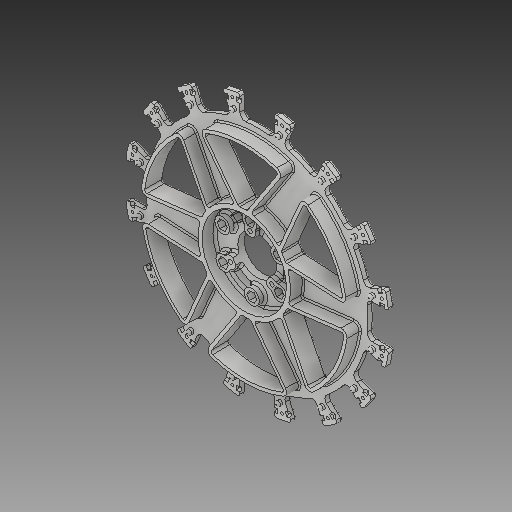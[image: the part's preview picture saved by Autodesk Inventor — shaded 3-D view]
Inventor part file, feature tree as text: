
AUTODESK INVENTOR PART (.ipt)
format: ipt  version: 2018 (Build 220112000, 112)  size: 1,820,160 bytes
history: native  units: in
note: dims shown in document units (in); Inventor stores cm internally (conversion verified against a paired STEP export)
features: fillet x1
ambient origin geometry x8: Origin, YZ Plane, XZ Plane, XY Plane, X Axis, Y Axis, Z Axis, Center Point
bodies: Solid1 (feature_tree)
feature tree (1):
  fillet  "Fillet16"  [1 undecoded]
note: 1 required parameter value undecoded (feature->parameter linkage not recoverable at this tier; creation-order binding heuristic only, values carry confidence <= 0.55)
